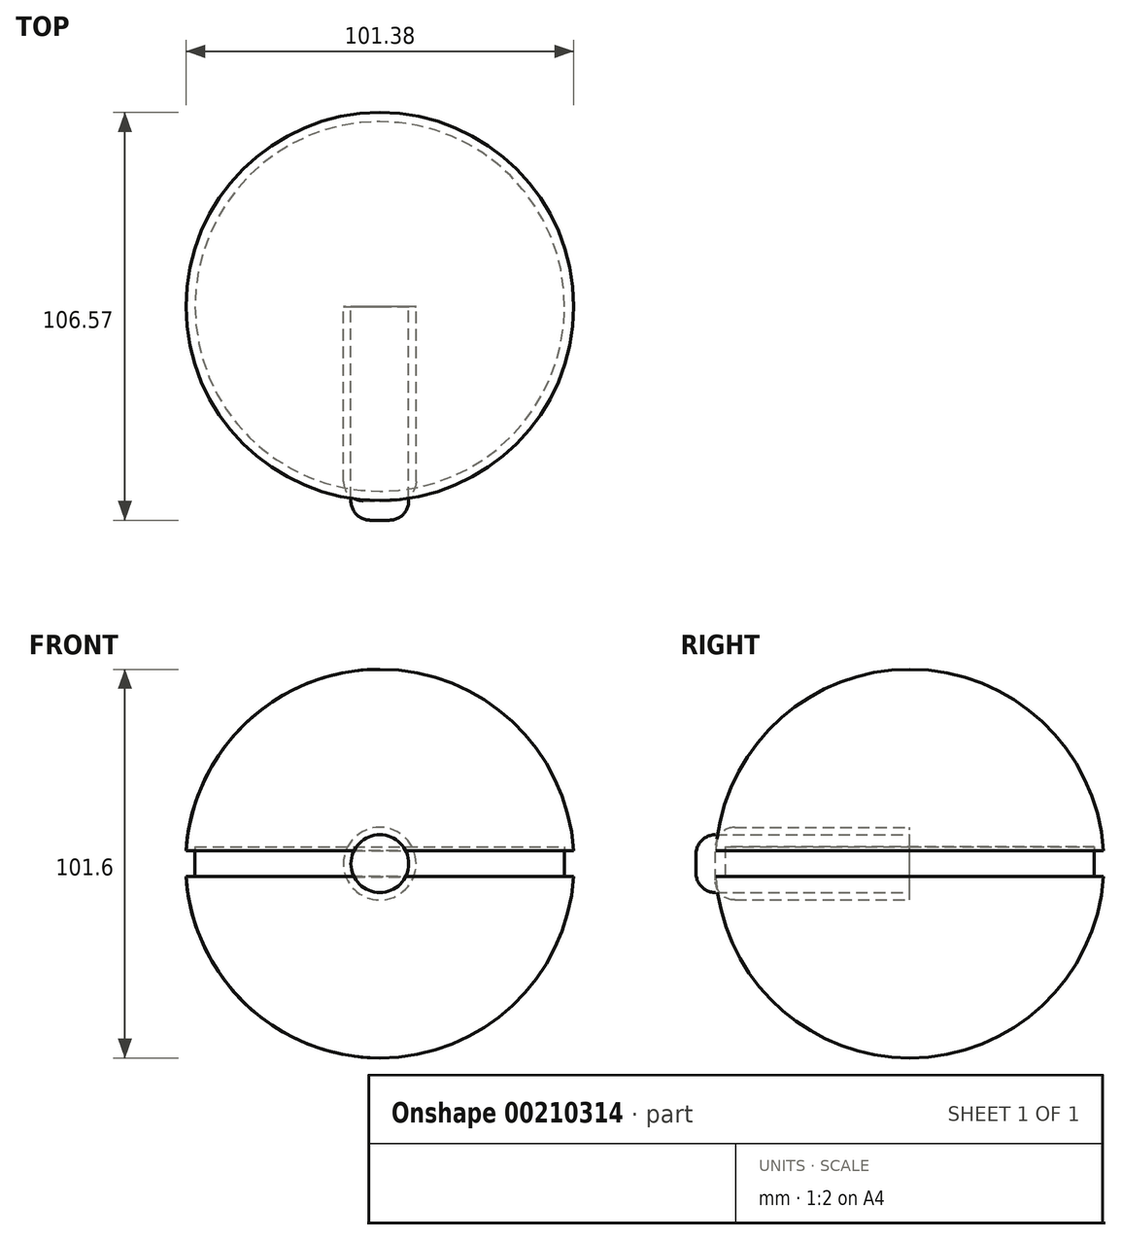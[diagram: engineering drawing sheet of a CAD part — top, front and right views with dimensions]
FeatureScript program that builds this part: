
annotation { "Feature Type Name" : "Feature", "Feature Type Description" : "" }
export const myFeature = defineFeature(function(context is Context, id is Id, definition is map)
    precondition{}
    {
        {
            var Q0;
            Q0=qCreatedBy(makeId("Front.planeOp"),FACE);
            var sketch = newSketch(context, id + "F0", { "sketchPlane" : qUnion([Q0])});
            skCircle(sketch, "E0", {"center": v(0, 0) * mm, "radius": 50.8 * mm});
            skLineSegment(sketch, "E1", {"start": v(0, 55.95) * mm, "end": v(0, -58.35) * mm});
            skLineSegment(sketch, "E2", {"start": v(-56.95, 3.4) * mm, "end": v(57.75, 3.4) * mm});
            skLineSegment(sketch, "E3", {"start": v(-57.35, -3.4) * mm, "end": v(57.35, -3.4) * mm});
            skSolve(sketch);
        }
        {
            var Q0;
            {var subQ0=sQuery(id+"F0.wireOp",EDGE,"E1");var subQ1=sQuery(id+"F0.wireOp",EDGE,"E0");var subQ2=makeQuery(id+"F0.imprint","INTERSECT",VERTEX,{"disambiguationData":[OD(0.0)],"derivedFrom":[subQ1,subQ0]});Q0=makeQuery(id+"F0.imprint","IMPRINT",FACE,{"disambiguationData":[TD([[makeQuery(id+"F0.imprint","IMPRINT",EDGE,{"disambiguationData":[TD([[subQ2,-1.0]])],"derivedFrom":subQ1}),1.0]])]});}
            var Q1;
            {var subQ0=sQuery(id+"F0.wireOp",EDGE,"E3");var subQ1=sQuery(id+"F0.wireOp",EDGE,"E0");var subQ2=makeQuery(id+"F0.imprint","INTERSECT",VERTEX,{"disambiguationData":[OD(0.0)],"derivedFrom":[subQ1,subQ0]});Q1=makeQuery(id+"F0.imprint","IMPRINT",FACE,{"disambiguationData":[TD([[makeQuery(id+"F0.imprint","IMPRINT",EDGE,{"disambiguationData":[TD([[subQ2,-1.0]])],"derivedFrom":subQ1}),1.0]])]});}
            var Q2;
            Q2=sQuery(id+"F0.wireOp",EDGE,"E1");
            revolve(context, id + "F1", {"entities" : qUnion([Q0, Q1]), "axis" : qUnion([Q2]), "revolveType" : RevolveType.FULL});
        }
        {
            var Q0;
            Q0=qCreatedBy(makeId("Front.planeOp"),FACE);
            var sketch = newSketch(context, id + "F2", { "sketchPlane" : qUnion([Q0])});
            skLineSegment(sketch, "E4.bottom", {"start": v(0, 4.42) * mm, "end": v(-48.32, 4.42) * mm});
            skLineSegment(sketch, "E4.top", {"start": v(0, -3.53) * mm, "end": v(-48.32, -3.53) * mm});
            skLineSegment(sketch, "E4.left", {"start": v(0, 4.42) * mm, "end": v(0, -3.53) * mm});
            skLineSegment(sketch, "E4.right", {"start": v(-48.32, 4.42) * mm, "end": v(-48.32, -3.53) * mm});
            skLineSegment(sketch, "E5.bottom", {"start": v(0, -3.53) * mm, "end": v(50.86, -3.53) * mm});
            skLineSegment(sketch, "E5.top", {"start": v(0, 3.67) * mm, "end": v(50.86, 3.67) * mm});
            skLineSegment(sketch, "E5.left", {"start": v(0, -3.53) * mm, "end": v(0, 3.67) * mm});
            skLineSegment(sketch, "E5.right", {"start": v(50.86, -3.53) * mm, "end": v(50.86, 3.67) * mm});
            skSolve(sketch);
        }
        {
            var Q0;
            Q0=makeQuery(id+"F2.imprint","IMPRINT",FACE,{"disambiguationData":[TD([[makeQuery(id+"F2.imprint","IMPRINT",EDGE,{"derivedFrom":sQuery(id+"F2.wireOp",EDGE,"E4.bottom")}),1.0]])]});
            var Q1;
            Q1=sQuery(id+"F2.wireOp",EDGE,"E5.left");
            revolve(context, id + "F3", {"entities" : qUnion([Q0]), "axis" : qUnion([Q1]), "revolveType" : RevolveType.FULL});
        }
        {
            var Q0;
            Q0=qCreatedBy(makeId("Front.planeOp"),FACE);
            var sketch = newSketch(context, id + "F4", { "sketchPlane" : qUnion([Q0])});
            skCircle(sketch, "E6", {"center": v(0, 0) * mm, "radius": 9.5 * mm});
            skSolve(sketch);
        }
        {
            var Q0;
            Q0 = qSketchRegion(id + "F4", true);
            extrude(context, id + "F5", {"entities" : qUnion([Q0]), "depth" : 50.8 * mm});
        }
        {
            var Q0;
            Q0=qCreatedBy(makeId("Front.planeOp"),FACE);
            var sketch = newSketch(context, id + "F6", { "sketchPlane" : qUnion([Q0])});
            skCircle(sketch, "E7", {"center": v(0, 0) * mm, "radius": 7.56 * mm});
            skSolve(sketch);
        }
        {
            var Q0;
            Q0 = qSketchRegion(id + "F6", true);
            extrude(context, id + "F7", {"entities" : qUnion([Q0]), "depth" : 55.88 * mm});
        }
        {
            var Q0;
            Q0=makeQuery(id+"F7.opExtrude","CAP_FACE",FACE,{"disambiguationData":[OSD([sQuery(id+"F6.wireOp",EDGE,"E7")])],"isStart":false});
            var Q1;
            Q1=makeQuery(id+"F5.opExtrude","CAP_EDGE",EDGE,{"disambiguationData":[OSD([sQuery(id+"F4.wireOp",EDGE,"E6")])],"isStart":false});
            fillet(context, id + "F8", {"entities" : qUnion([Q0, Q1]), "radius" : 5.08 * mm, "tangentPropagation" : true, "allowEdgeOverflow" : false});
        }
    });
